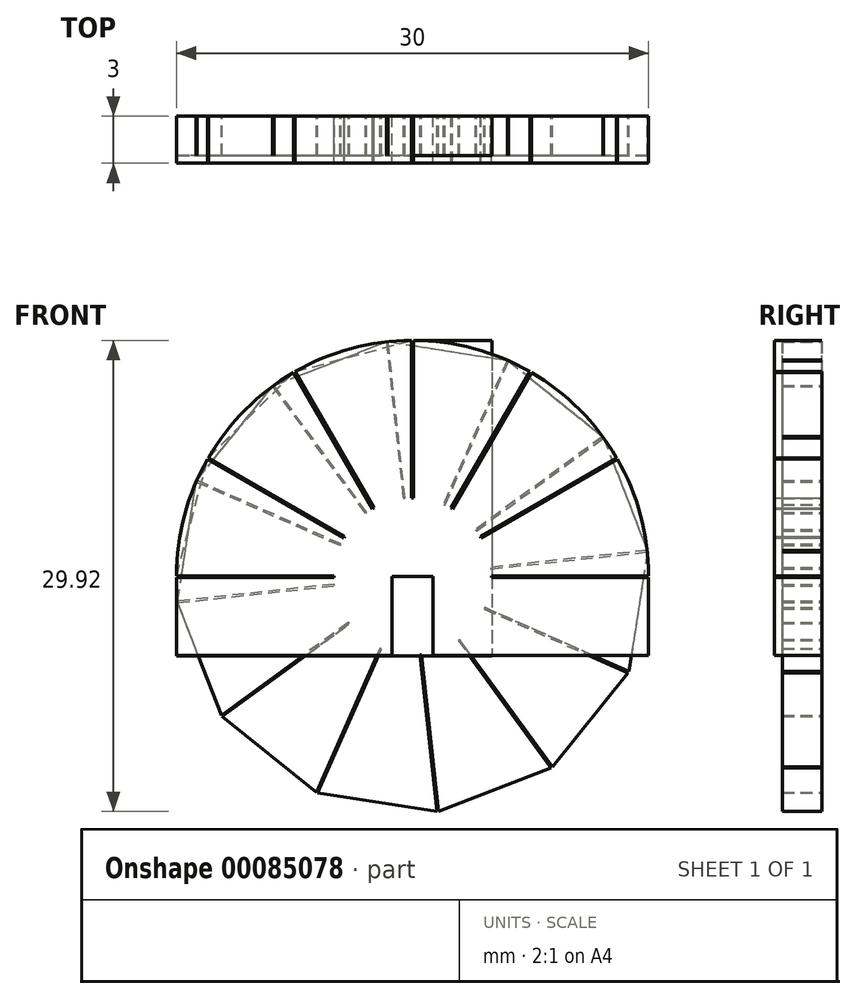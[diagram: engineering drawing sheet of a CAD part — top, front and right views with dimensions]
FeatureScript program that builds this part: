
annotation { "Feature Type Name" : "Feature", "Feature Type Description" : "" }
export const myFeature = defineFeature(function(context is Context, id is Id, definition is map)
    precondition{}
    {
        {
            var Q0;
            Q0=qCreatedBy(makeId("Front.planeOp"),FACE);
            var sketch = newSketch(context, id + "F0", { "sketchPlane" : qUnion([Q0])});
            skArc(sketch, "E0", {"start": v(-15, 0) * mm, "mid": v(0, 15) * mm, "end": v(15, 0) * mm, "construction": true});
            skLineSegment(sketch, "E1", {"start": v(-0.05, 15) * mm, "end": v(-0.05, 5) * mm});
            skLineSegment(sketch, "E2", {"start": v(0.05, 15) * mm, "end": v(0.05, 5) * mm});
            skLineSegment(sketch, "E3", {"start": v(-0.05, 5) * mm, "end": v(0.05, 5) * mm});
            skLineSegment(sketch, "E4", {"start": v(15, 0.05) * mm, "end": v(5, 0.05) * mm});
            skLineSegment(sketch, "E5", {"start": v(5, 0.05) * mm, "end": v(5, -0.05) * mm});
            skLineSegment(sketch, "E6", {"start": v(5, -0.05) * mm, "end": v(15, -0.05) * mm});
            skLineSegment(sketch, "E7", {"start": v(15, -0.05) * mm, "end": v(15, -5) * mm});
            skLineSegment(sketch, "E8", {"start": v(-15, -5) * mm, "end": v(-15, -0.05) * mm});
            skLineSegment(sketch, "E9", {"start": v(-15, -0.05) * mm, "end": v(-5, -0.05) * mm});
            skLineSegment(sketch, "E10", {"start": v(-5, -0.05) * mm, "end": v(-5, 0.05) * mm});
            skLineSegment(sketch, "E11", {"start": v(-5, 0.05) * mm, "end": v(-15, 0.05) * mm});
            skArc(sketch, "E12", {"start": v(-5, 0) * mm, "mid": v(0, 5) * mm, "end": v(5, 0) * mm, "construction": true});
            skLineSegment(sketch, "E13", {"start": v(0, 0) * mm, "end": v(7.5, 13) * mm, "construction": true});
            skLineSegment(sketch, "E14", {"start": v(7.54, 12.97) * mm, "end": v(2.54, 4.3) * mm});
            skLineSegment(sketch, "E15", {"start": v(2.46, 4.35) * mm, "end": v(2.54, 4.3) * mm});
            skLineSegment(sketch, "E16", {"start": v(2.46, 4.35) * mm, "end": v(7.46, 13.02) * mm});
            skLineSegment(sketch, "E17", {"start": v(4.3, 2.54) * mm, "end": v(4.35, 2.46) * mm});
            skLineSegment(sketch, "E18", {"start": v(13.02, 7.46) * mm, "end": v(4.35, 2.46) * mm});
            skLineSegment(sketch, "E19", {"start": v(4.3, 2.54) * mm, "end": v(12.97, 7.54) * mm});
            skLineSegment(sketch, "E20", {"start": v(0, 0) * mm, "end": v(13, 7.5) * mm, "construction": true});
            skArc(sketch, "E21", {"start": v(13.02, 7.46) * mm, "mid": v(14.49, 3.88) * mm, "end": v(15, 0.05) * mm});
            skArc(sketch, "E22", {"start": v(7.54, 12.97) * mm, "mid": v(10.6, 10.6) * mm, "end": v(12.97, 7.54) * mm});
            skArc(sketch, "E23", {"start": v(0.05, 15) * mm, "mid": v(3.88, 14.49) * mm, "end": v(7.46, 13.02) * mm});
            skLineSegment(sketch, "E24", {"start": v(0, 0) * mm, "end": v(-13, 7.5) * mm, "construction": true});
            skLineSegment(sketch, "E25", {"start": v(-13.02, 7.46) * mm, "end": v(-4.35, 2.46) * mm});
            skLineSegment(sketch, "E26", {"start": v(-4.35, 2.46) * mm, "end": v(-4.3, 2.54) * mm});
            skLineSegment(sketch, "E27", {"start": v(-4.3, 2.54) * mm, "end": v(-12.97, 7.54) * mm});
            skLineSegment(sketch, "E28", {"start": v(0, 0) * mm, "end": v(-7.5, 13) * mm, "construction": true});
            skLineSegment(sketch, "E29", {"start": v(-7.54, 12.97) * mm, "end": v(-2.54, 4.3) * mm});
            skLineSegment(sketch, "E30", {"start": v(-2.46, 4.35) * mm, "end": v(-7.46, 13.02) * mm});
            skLineSegment(sketch, "E31", {"start": v(-2.54, 4.3) * mm, "end": v(-2.46, 4.35) * mm});
            skArc(sketch, "E32", {"start": v(-15, 0.05) * mm, "mid": v(-14.49, 3.88) * mm, "end": v(-13.02, 7.46) * mm});
            skArc(sketch, "E33", {"start": v(-12.97, 7.54) * mm, "mid": v(-10.6, 10.6) * mm, "end": v(-7.54, 12.97) * mm});
            skArc(sketch, "E34", {"start": v(-7.46, 13.02) * mm, "mid": v(-3.88, 14.49) * mm, "end": v(-0.05, 15) * mm});
            skLineSegment(sketch, "E35", {"start": v(-15, -5) * mm, "end": v(-1.3, -5) * mm});
            skLineSegment(sketch, "E36", {"start": v(-1.3, -5) * mm, "end": v(-1.3, 0) * mm});
            skLineSegment(sketch, "E37", {"start": v(-1.3, 0) * mm, "end": v(1.3, 0) * mm});
            skLineSegment(sketch, "E38", {"start": v(1.3, 0) * mm, "end": v(1.3, -5) * mm});
            skLineSegment(sketch, "E39", {"start": v(1.3, -5) * mm, "end": v(15, -5) * mm});
            skSolve(sketch);
        }
        {
            var Q0;
            Q0=qSketchRegion(id+"F0",true);
            extrude(context, id + "F1", {"entities" : qUnion([Q0]), "depth" : 3 * mm});
        }
        {
            var Q0;
            Q0=qCreatedBy(makeId("Front.planeOp"),FACE);
            var sketch = newSketch(context, id + "F2", { "sketchPlane" : qUnion([Q0])});
            skCircle(sketch, "E40", {"center": v(0, 0) * mm, "radius": 15 * mm, "construction": true});
            skCircle(sketch, "E41", {"center": v(0, 0) * mm, "radius": 5 * mm, "construction": true});
            skLineSegment(sketch, "E42", {"start": v(-1.66, 14.9) * mm, "end": v(-0.59, 4.97) * mm});
            skLineSegment(sketch, "E43", {"start": v(-0.59, 4.97) * mm, "end": v(-0.49, 4.98) * mm});
            skLineSegment(sketch, "E44", {"start": v(-0.49, 4.98) * mm, "end": v(-1.56, 14.92) * mm});
            skLineSegment(sketch, "E45.1.0", {"start": v(-2.9, 4.07) * mm, "end": v(-8.8, 12.14) * mm});
            skLineSegment(sketch, "E45.1.1", {"start": v(-2.99, 4) * mm, "end": v(-2.9, 4.07) * mm});
            skLineSegment(sketch, "E45.1.2", {"start": v(-8.89, 12.08) * mm, "end": v(-2.99, 4) * mm});
            skLineSegment(sketch, "E45.2.0", {"start": v(-4.55, 2.07) * mm, "end": v(-13.7, 6.11) * mm});
            skLineSegment(sketch, "E45.2.1", {"start": v(-4.6, 1.98) * mm, "end": v(-4.55, 2.07) * mm});
            skLineSegment(sketch, "E45.2.2", {"start": v(-13.74, 6.02) * mm, "end": v(-4.6, 1.98) * mm});
            skLineSegment(sketch, "E46.1.3.0", {"start": v(-4.98, -0.49) * mm, "end": v(-14.92, -1.56) * mm});
            skLineSegment(sketch, "E46.3.3.0", {"start": v(-4.97, -0.59) * mm, "end": v(-4.98, -0.49) * mm});
            skLineSegment(sketch, "E46.6.3.0", {"start": v(-14.9, -1.66) * mm, "end": v(-4.97, -0.59) * mm});
            skLineSegment(sketch, "E46.1.4.0", {"start": v(-4.07, -2.9) * mm, "end": v(-12.14, -8.8) * mm});
            skLineSegment(sketch, "E46.3.4.0", {"start": v(-4, -2.99) * mm, "end": v(-4.07, -2.9) * mm});
            skLineSegment(sketch, "E46.6.4.0", {"start": v(-12.08, -8.89) * mm, "end": v(-4, -2.99) * mm});
            skLineSegment(sketch, "E46.1.5.0", {"start": v(-2.07, -4.55) * mm, "end": v(-6.11, -13.7) * mm});
            skLineSegment(sketch, "E46.3.5.0", {"start": v(-1.98, -4.6) * mm, "end": v(-2.07, -4.55) * mm});
            skLineSegment(sketch, "E46.6.5.0", {"start": v(-6.02, -13.74) * mm, "end": v(-1.98, -4.6) * mm});
            skLineSegment(sketch, "E46.1.6.0", {"start": v(0.49, -4.98) * mm, "end": v(1.56, -14.92) * mm});
            skLineSegment(sketch, "E46.3.6.0", {"start": v(0.59, -4.97) * mm, "end": v(0.49, -4.98) * mm});
            skLineSegment(sketch, "E46.6.6.0", {"start": v(1.66, -14.9) * mm, "end": v(0.59, -4.97) * mm});
            skLineSegment(sketch, "E46.1.7.0", {"start": v(2.9, -4.07) * mm, "end": v(8.8, -12.14) * mm});
            skLineSegment(sketch, "E46.3.7.0", {"start": v(2.99, -4) * mm, "end": v(2.9, -4.07) * mm});
            skLineSegment(sketch, "E46.6.7.0", {"start": v(8.89, -12.08) * mm, "end": v(2.99, -4) * mm});
            skLineSegment(sketch, "E46.1.8.0", {"start": v(4.55, -2.07) * mm, "end": v(13.7, -6.1) * mm});
            skLineSegment(sketch, "E46.3.8.0", {"start": v(4.6, -1.98) * mm, "end": v(4.55, -2.07) * mm});
            skLineSegment(sketch, "E46.6.8.0", {"start": v(13.74, -6.02) * mm, "end": v(4.6, -1.98) * mm});
            skLineSegment(sketch, "E46.1.9.0", {"start": v(4.98, 0.49) * mm, "end": v(14.92, 1.56) * mm});
            skLineSegment(sketch, "E46.3.9.0", {"start": v(4.97, 0.59) * mm, "end": v(4.98, 0.49) * mm});
            skLineSegment(sketch, "E46.6.9.0", {"start": v(14.9, 1.66) * mm, "end": v(4.97, 0.59) * mm});
            skLineSegment(sketch, "E46.1.10.0", {"start": v(4.07, 2.9) * mm, "end": v(12.14, 8.8) * mm});
            skLineSegment(sketch, "E46.3.10.0", {"start": v(4, 3) * mm, "end": v(4.07, 2.9) * mm});
            skLineSegment(sketch, "E46.6.10.0", {"start": v(12.08, 8.89) * mm, "end": v(4, 3) * mm});
            skLineSegment(sketch, "E46.1.11.0", {"start": v(2.07, 4.55) * mm, "end": v(6.11, 13.7) * mm});
            skLineSegment(sketch, "E46.3.11.0", {"start": v(1.98, 4.6) * mm, "end": v(2.07, 4.55) * mm});
            skLineSegment(sketch, "E46.6.11.0", {"start": v(6.02, 13.74) * mm, "end": v(1.98, 4.6) * mm});
            skLineSegment(sketch, "E47", {"start": v(-8.8, 12.14) * mm, "end": v(-1.66, 14.9) * mm});
            skLineSegment(sketch, "E48", {"start": v(-1.56, 14.92) * mm, "end": v(6.02, 13.74) * mm});
            skLineSegment(sketch, "E49", {"start": v(6.11, 13.7) * mm, "end": v(12.08, 8.89) * mm});
            skLineSegment(sketch, "E50", {"start": v(12.14, 8.8) * mm, "end": v(14.9, 1.66) * mm});
            skLineSegment(sketch, "E51", {"start": v(14.92, 1.56) * mm, "end": v(13.74, -6.02) * mm});
            skLineSegment(sketch, "E52", {"start": v(13.7, -6.1) * mm, "end": v(8.89, -12.08) * mm});
            skLineSegment(sketch, "E53", {"start": v(8.8, -12.14) * mm, "end": v(1.66, -14.9) * mm});
            skLineSegment(sketch, "E54", {"start": v(1.56, -14.92) * mm, "end": v(-6.02, -13.74) * mm});
            skLineSegment(sketch, "E55", {"start": v(-6.11, -13.7) * mm, "end": v(-12.08, -8.89) * mm});
            skLineSegment(sketch, "E56", {"start": v(-12.14, -8.8) * mm, "end": v(-14.9, -1.66) * mm});
            skLineSegment(sketch, "E57", {"start": v(-14.92, -1.56) * mm, "end": v(-13.74, 6.02) * mm});
            skLineSegment(sketch, "E58", {"start": v(-13.7, 6.11) * mm, "end": v(-8.89, 12.08) * mm});
            skSolve(sketch);
        }
        {
            var Q0;
            Q0=qSketchRegion(id+"F2",true);
            extrude(context, id + "F3", {"entities" : qUnion([Q0]), "depth" : 2.5 * mm});
        }
        {
            var Q0;
            Q0=qCreatedBy(makeId("Front.planeOp"),FACE);
            var sketch = newSketch(context, id + "F4", { "sketchPlane" : qUnion([Q0])});
            skArc(sketch, "E59", {"start": v(-15, 0) * mm, "mid": v(-10.6, 10.6) * mm, "end": v(0, 15) * mm, "construction": true});
            skArc(sketch, "E60", {"start": v(-5, 0) * mm, "mid": v(-3.54, 3.54) * mm, "end": v(0, 5) * mm, "construction": true});
            skLineSegment(sketch, "E61", {"start": v(-15, -0.05) * mm, "end": v(-5, -0.05) * mm});
            skLineSegment(sketch, "E62", {"start": v(-5, -0.05) * mm, "end": v(-5, 0.05) * mm});
            skLineSegment(sketch, "E63", {"start": v(-5, 0.05) * mm, "end": v(-15, 0.05) * mm});
            skLineSegment(sketch, "E64", {"start": v(-15, 0.05) * mm, "end": v(-13.02, 7.46) * mm});
            skLineSegment(sketch, "E65", {"start": v(-13.02, 7.46) * mm, "end": v(-4.35, 2.46) * mm});
            skLineSegment(sketch, "E66", {"start": v(-4.3, 2.54) * mm, "end": v(-12.97, 7.54) * mm});
            skLineSegment(sketch, "E67", {"start": v(-12.97, 7.54) * mm, "end": v(-7.54, 12.97) * mm});
            skLineSegment(sketch, "E68", {"start": v(-7.54, 12.97) * mm, "end": v(-2.54, 4.3) * mm});
            skLineSegment(sketch, "E69", {"start": v(-2.54, 4.3) * mm, "end": v(-2.46, 4.35) * mm});
            skLineSegment(sketch, "E70", {"start": v(-2.46, 4.35) * mm, "end": v(-7.46, 13.02) * mm});
            skLineSegment(sketch, "E71", {"start": v(-7.46, 13.02) * mm, "end": v(-0.05, 15) * mm});
            skLineSegment(sketch, "E72", {"start": v(-0.05, 15) * mm, "end": v(-0.05, 5) * mm});
            skLineSegment(sketch, "E73", {"start": v(-0.05, 5) * mm, "end": v(0.05, 5) * mm});
            skLineSegment(sketch, "E74", {"start": v(0.05, 5) * mm, "end": v(0.05, 15) * mm});
            skLineSegment(sketch, "E75", {"start": v(0.05, 15) * mm, "end": v(5.05, 15) * mm});
            skLineSegment(sketch, "E76", {"start": v(5.05, 15) * mm, "end": v(5.05, -5.05) * mm});
            skLineSegment(sketch, "E77", {"start": v(5.05, -5.05) * mm, "end": v(-15, -5.05) * mm});
            skLineSegment(sketch, "E78", {"start": v(-15, -5.05) * mm, "end": v(-15, -0.05) * mm});
            skLineSegment(sketch, "E79", {"start": v(0, 0) * mm, "end": v(-13, 7.5) * mm, "construction": true});
            skLineSegment(sketch, "E80", {"start": v(0, 0) * mm, "end": v(-7.5, 13) * mm, "construction": true});
            skLineSegment(sketch, "E81", {"start": v(-4.3, 2.54) * mm, "end": v(-4.35, 2.46) * mm});
            skLineSegment(sketch, "E82", {"start": v(-15, -0.05) * mm, "end": v(-15, 0.05) * mm, "construction": true});
            skLineSegment(sketch, "E83", {"start": v(0.05, 15) * mm, "end": v(-0.05, 15) * mm, "construction": true});
            skSolve(sketch);
        }
        {
            var Q0;
            Q0=qSketchRegion(id+"F4",true);
            extrude(context, id + "F5", {"entities" : qUnion([Q0]), "depth" : 2.5 * mm});
        }
    });
